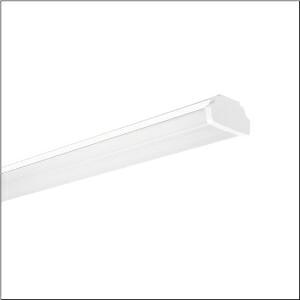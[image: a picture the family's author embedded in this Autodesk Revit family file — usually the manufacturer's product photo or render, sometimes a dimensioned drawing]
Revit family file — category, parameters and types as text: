
# Revit family: modario_r__31_ho_53bm811d2v4120_c329
name_source: partatom
category: Lighting Fixtures
units: mm (PartAtom-declared; Revit-internal decimal feet)

## family parameters
Cut with Voids When Loaded = No
Host = Face
Light Source = No
Part Type = Normal
Room Calculation Point = No
Round Connector Dimension = Use Diameter
Shared = No

## types (1)
- --- (1 x LED, 12350 lm, 79.5 W, 4000K)
    Apparent Load = 80 VA
    CIE Flux Codes = 52 78 94 90 100
    Color Rendering = 80
    Color Temperature = 4000K
    Default Elevation = 1800 mm
    Description = Modario® 31 HO, luminaire insert, of sheet steel, coil coated, white, length: 1.495mm, width: 81mm, height: 82mm, 5x system unit, system units: 299mm, LED rated luminous flux: 12.350lm, light colour: 840, control gear: DALI 2, control gear: ECG DALI, with plug, 5-pole, with phase selection, mains connection: 220..240V, AC, 50/60Hz, rated input power: 79W, through-wiring accessed according to module size, primary optical cover: cover, of PMMA, light emission: direct distribution, primary light characteristic: symmetric, protection rating (complete): IP20, protection rating (LED compartment): IP50, insulation class (complete): insulation class I (protective earthing), certification: CE, ENEC, VDE, UKCA, impact resistance: IK03, permissible ambient temperature for indoor applications: -25..+30°C, corresponds to IFS (International Featured Standards) requirements for safety and quality in the food industry, reducing of maximum allowable ambient temperature of 5°C with ceiling mounting, packaging unit: 1 piece
    Height = 92 mm
    Lamp = 1 x LED
    Lamp Light Flux = 12350 lm
    Lamp Power = 79.5 W
    Lamp count = 1
    Length = 1495 mm
    Luminous efficacy = 155 lm/W
    Manufacturer = Siteco
    ModVariant = No
    Model = 53BM811D2V4120
    Mounting Place = Ceiling
    Mounting Type = Pendant
    Number of Poles = 1
    OnlyDefault = Yes
    Power Factor = 1
    Product Name = Modario® 31 HO
    Product group = luminaire insert
    ProductGroupID = 901
    Protection Class = Protection class I
    Protection Degree = IP 20
    RLX_Detail_Level = 1
    RLX_Emergency_Light_Flux = 0 lm
    RLX_Emergency_Type = 0
    RLX_Emergency_Type_DB = No
    RlxData = <blob elided: 42253 chars, md5=4b47bbad>
    Socket = socket
    Standby Power = 0 W
    System Light Flux = 12350 lm
    System Power = 80 W
    Type Comments = factory setting: luminous flux: 100 % | dim-lin: 254 | 345 mA
    Type Image = l_1300283.jpg
    URL = http://relux.com
    VarID = @adj_135241
    Voltage = 0 V
    Weight = 0.00 kg
    Width = 81 mm

## geometry (parser evidence)
native form markers: Blend x4, Sweep x12
no freeform markers — native parametric forms only
